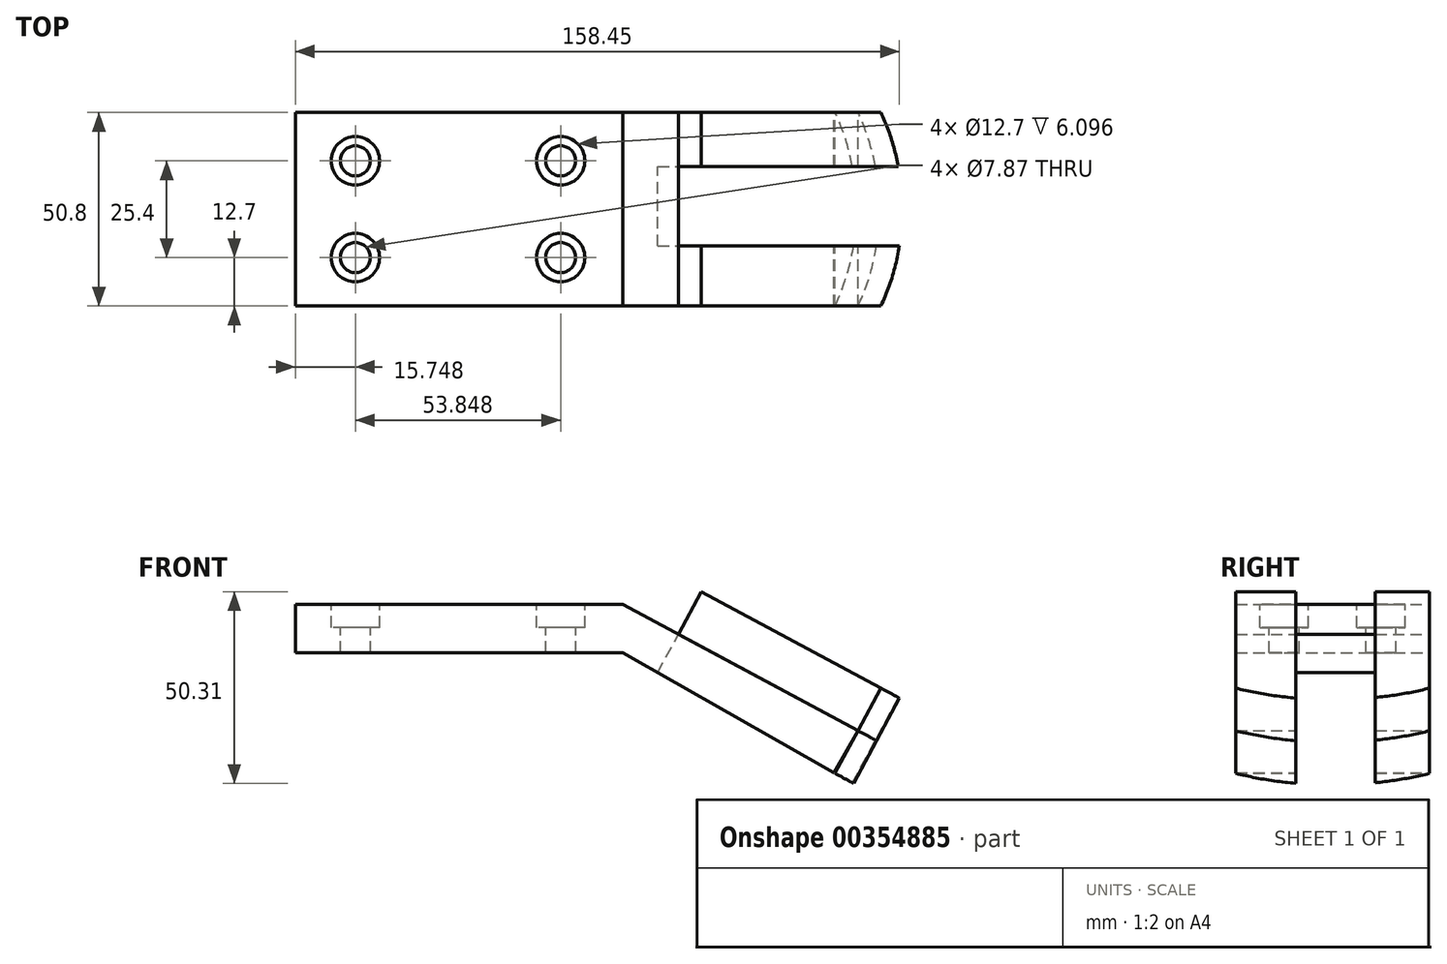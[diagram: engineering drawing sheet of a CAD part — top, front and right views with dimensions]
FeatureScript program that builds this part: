
annotation { "Feature Type Name" : "Feature", "Feature Type Description" : "" }
export const myFeature = defineFeature(function(context is Context, id is Id, definition is map)
    precondition{}
    {
        {
            var Q0;
            Q0=qCreatedBy(makeId("Front.planeOp"),FACE);
            var sketch = newSketch(context, id + "F0", { "sketchPlane" : qUnion([Q0])});
            skLineSegment(sketch, "E0", {"start": v(0, 0) * mm, "end": v(0, 12.7) * mm});
            skLineSegment(sketch, "E1", {"start": v(0, 0) * mm, "end": v(85.85, 0) * mm});
            skLineSegment(sketch, "E2", {"start": v(85.85, 0) * mm, "end": v(141.31, -31.55) * mm});
            skLineSegment(sketch, "E3", {"start": v(0, 12.7) * mm, "end": v(85.85, 12.7) * mm});
            skLineSegment(sketch, "E4", {"start": v(141.31, -31.55) * mm, "end": v(147.6, -20.5) * mm});
            skLineSegment(sketch, "E5", {"start": v(147.6, -20.5) * mm, "end": v(85.85, 12.7) * mm});
            skSolve(sketch);
        }
        {
            var Q0;
            Q0 = qSketchRegion(id + "F0", true);
            extrude(context, id + "F1", {"entities" : qUnion([Q0]), "depth" : 50.8 * mm});
        }
        {
            var Q0;
            Q0=makeQuery(id+"F1.opExtrude","SWEPT_FACE",FACE,{"disambiguationData":[OSD([sQuery(id+"F0.wireOp",EDGE,"E3")])]});
            var sketch = newSketch(context, id + "F2", { "sketchPlane" : qUnion([Q0])});
            skCircle(sketch, "E6", {"center": v(15.75, -12.7) * mm, "radius": 6.35 * mm});
            skCircle(sketch, "E7", {"center": v(69.6, -12.7) * mm, "radius": 6.35 * mm});
            skCircle(sketch, "E8", {"center": v(15.75, -38.1) * mm, "radius": 6.35 * mm});
            skCircle(sketch, "E9", {"center": v(69.6, -38.1) * mm, "radius": 6.35 * mm});
            skSolve(sketch);
        }
        {
            var Q0;
            Q0 = qSketchRegion(id + "F2", true);
            extrude(context, id + "F3", {"entities" : qUnion([Q0]), "operationType" : NewBodyOperationType.REMOVE, "oppositeDirection" : true, "depth" : 6.1 * mm});
        }
        {
            var Q0;
            Q0=makeQuery(id+"F1.opExtrude","SWEPT_FACE",FACE,{"disambiguationData":[OSD([sQuery(id+"F0.wireOp",EDGE,"E3")])]});
            var sketch = newSketch(context, id + "F4", { "sketchPlane" : qUnion([Q0])});
            skCircle(sketch, "E10", {"center": v(15.75, -12.7) * mm, "radius": 3.94 * mm});
            skCircle(sketch, "E11", {"center": v(69.6, -12.7) * mm, "radius": 3.94 * mm});
            skCircle(sketch, "E12", {"center": v(69.6, -38.1) * mm, "radius": 3.94 * mm});
            skCircle(sketch, "E13", {"center": v(15.75, -38.1) * mm, "radius": 3.94 * mm});
            skSolve(sketch);
        }
        {
            var Q0;
            Q0 = qSketchRegion(id + "F4", true);
            extrude(context, id + "F5", {"entities" : qUnion([Q0]), "operationType" : NewBodyOperationType.REMOVE, "endBound" : BoundingType.THROUGH_ALL, "oppositeDirection" : true, "depth" : 25.4 * mm});
        }
        {
            var Q0;
            Q0=makeQuery(id+"F1.opExtrude","SWEPT_FACE",FACE,{"disambiguationData":[OSD([sQuery(id+"F0.wireOp",EDGE,"E5")])]});
            var sketch = newSketch(context, id + "F6", { "sketchPlane" : qUnion([Q0])});
            skArc(sketch, "E14", {"start": v(139.7, -50.8) * mm, "mid": v(146.06, -25.4) * mm, "end": v(139.7, 0) * mm});
            skLineSegment(sketch, "E15", {"start": v(139.7, 0) * mm, "end": v(139.7, -50.8) * mm});
            skSolve(sketch);
        }
        {
            var Q0;
            Q0 = qSketchRegion(id + "F6", true);
            extrude(context, id + "F7", {"entities" : qUnion([Q0]), "oppositeDirection" : true, "depth" : 12.7 * mm});
        }
        {
            var Q0;
            Q0=makeQuery(id+"F1.opExtrude","SWEPT_FACE",FACE,{"disambiguationData":[OSD([sQuery(id+"F0.wireOp",EDGE,"E5")])]});
            var sketch = newSketch(context, id + "F8", { "sketchPlane" : qUnion([Q0])});
            skLineSegment(sketch, "E16.bottom", {"start": v(139.7, -50.8) * mm, "end": v(86.21, -50.8) * mm});
            skLineSegment(sketch, "E16.top", {"start": v(139.7, 0) * mm, "end": v(86.21, 0) * mm});
            skLineSegment(sketch, "E16.left", {"start": v(139.7, -50.8) * mm, "end": v(139.7, 0) * mm});
            skLineSegment(sketch, "E16.right", {"start": v(86.21, -50.8) * mm, "end": v(86.21, 0) * mm});
            skArc(sketch, "E17", {"start": v(139.7, -50.8) * mm, "mid": v(146.06, -25.4) * mm, "end": v(139.7, 0) * mm});
            skSolve(sketch);
        }
        {
            var Q0;
            Q0 = qSketchRegion(id + "F8", true);
            extrude(context, id + "F9", {"entities" : qUnion([Q0]), "depth" : 12.7 * mm});
        }
        {
            var Q0;
            Q0=makeQuery(id+"F9.opExtrude","CAP_FACE",FACE,{"disambiguationData":[OSD([sQuery(id+"F8.wireOp",EDGE,"E16.bottom"),sQuery(id+"F8.wireOp",EDGE,"E16.top"),sQuery(id+"F8.wireOp",EDGE,"E16.right"),sQuery(id+"F8.wireOp",EDGE,"E17")])],"isStart":false});
            var sketch = newSketch(context, id + "F10", { "sketchPlane" : qUnion([Q0])});
            skLineSegment(sketch, "E18.bottom", {"start": v(86.21, -35.05) * mm, "end": v(149.35, -35.05) * mm});
            skLineSegment(sketch, "E18.top", {"start": v(86.21, -14.2) * mm, "end": v(149.35, -14.2) * mm});
            skLineSegment(sketch, "E18.left", {"start": v(86.21, -35.05) * mm, "end": v(86.21, -14.2) * mm});
            skLineSegment(sketch, "E18.right", {"start": v(149.35, -35.05) * mm, "end": v(149.35, -14.2) * mm});
            skSolve(sketch);
        }
        {
            var Q0;
            Q0 = qSketchRegion(id + "F10", true);
            extrude(context, id + "F11", {"entities" : qUnion([Q0]), "operationType" : NewBodyOperationType.REMOVE, "oppositeDirection" : true, "depth" : 25.4 * mm});
        }
    });
